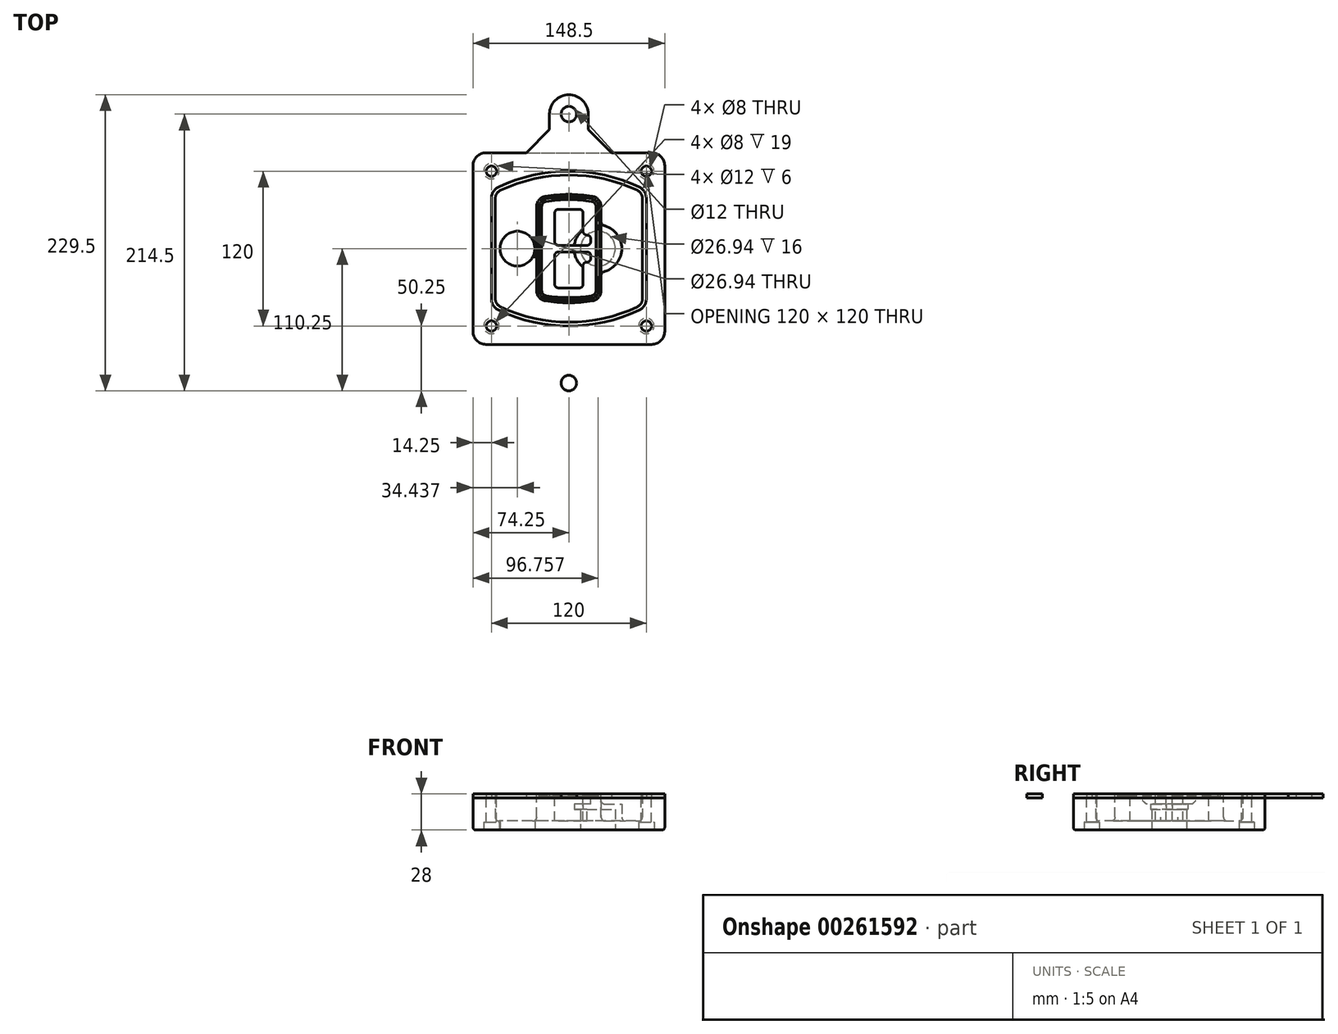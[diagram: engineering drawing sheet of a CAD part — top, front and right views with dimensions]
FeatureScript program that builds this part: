
annotation { "Feature Type Name" : "Feature", "Feature Type Description" : "" }
export const myFeature = defineFeature(function(context is Context, id is Id, definition is map)
    precondition{}
    {
        {
            var Q0;
            Q0=qCreatedBy(makeId("Top.planeOp"),FACE);
            var sketch = newSketch(context, id + "F0", { "sketchPlane" : qUnion([Q0])});
            skPoint(sketch, "E0.rect.middle", {"position": v(0, 0) * mm});
            skLineSegment(sketch, "E1.bottom", {"start": v(-64.25, -74.25) * mm, "end": v(64.25, -74.25) * mm});
            skLineSegment(sketch, "E1.top", {"start": v(-64.25, 74.25) * mm, "end": v(64.25, 74.25) * mm});
            skLineSegment(sketch, "E1.left", {"start": v(-74.25, -64.25) * mm, "end": v(-74.25, 64.25) * mm});
            skLineSegment(sketch, "E1.right", {"start": v(74.25, -64.25) * mm, "end": v(74.25, 64.25) * mm});
            skLineSegment(sketch, "E2", {"start": v(-74.25, 74.25) * mm, "end": v(74.25, -74.25) * mm, "construction": true});
            skLineSegment(sketch, "E3", {"start": v(74.25, 74.25) * mm, "end": v(-74.25, -74.25) * mm, "construction": true});
            skCircle(sketch, "E4", {"center": v(-60, 60) * mm, "radius": 4 * mm});
            skCircle(sketch, "E5", {"center": v(60, 60) * mm, "radius": 4 * mm});
            skCircle(sketch, "E6", {"center": v(60, -60) * mm, "radius": 4 * mm});
            skCircle(sketch, "E7", {"center": v(-60, -60) * mm, "radius": 4 * mm});
            skLineSegment(sketch, "E8", {"start": v(-60, 60) * mm, "end": v(60, 60) * mm, "construction": true});
            skLineSegment(sketch, "E9", {"start": v(60, 60) * mm, "end": v(60, -60) * mm, "construction": true});
            skLineSegment(sketch, "E10", {"start": v(60, -60) * mm, "end": v(-60, -60) * mm, "construction": true});
            skLineSegment(sketch, "E11", {"start": v(-60, -60) * mm, "end": v(-60, 60) * mm, "construction": true});
            skLineSegment(sketch, "E12", {"start": v(-60, 38.83) * mm, "end": v(-60, -38.83) * mm});
            skLineSegment(sketch, "E13", {"start": v(60, 38.83) * mm, "end": v(60, -38.83) * mm});
            skArc(sketch, "E14", {"start": v(54.26, 47.88) * mm, "mid": v(0, 60) * mm, "end": v(-54.26, 47.88) * mm});
            skArc(sketch, "E15", {"start": v(-54.26, -47.88) * mm, "mid": v(0, -60) * mm, "end": v(54.26, -47.88) * mm});
            skLineSegment(sketch, "E16", {"start": v(-60, 0) * mm, "end": v(60, 0) * mm, "construction": true});
            skPoint(sketch, "E17.visualSharp", {"position": v(-60, -45) * mm});
            skArc(sketch, "E17.filletArc", {"start": v(-60, -38.83) * mm, "mid": v(-58.44, -44.2) * mm, "end": v(-54.26, -47.88) * mm});
            skPoint(sketch, "E18.visualSharp", {"position": v(-60, 45) * mm});
            skArc(sketch, "E18.filletArc", {"start": v(-54.26, 47.88) * mm, "mid": v(-58.44, 44.2) * mm, "end": v(-60, 38.83) * mm});
            skPoint(sketch, "E19.visualSharp", {"position": v(60, 45) * mm});
            skArc(sketch, "E19.filletArc", {"start": v(60, 38.83) * mm, "mid": v(58.44, 44.2) * mm, "end": v(54.26, 47.88) * mm});
            skPoint(sketch, "E20.visualSharp", {"position": v(60, -45) * mm});
            skArc(sketch, "E20.filletArc", {"start": v(54.26, -47.88) * mm, "mid": v(58.44, -44.2) * mm, "end": v(60, -38.83) * mm});
            skPoint(sketch, "E21.visualSharp", {"position": v(-74.25, 74.25) * mm});
            skArc(sketch, "E21.filletArc", {"start": v(-64.25, 74.25) * mm, "mid": v(-71.32, 71.32) * mm, "end": v(-74.25, 64.25) * mm});
            skPoint(sketch, "E22.visualSharp", {"position": v(74.25, 74.25) * mm});
            skArc(sketch, "E22.filletArc", {"start": v(74.25, 64.25) * mm, "mid": v(71.32, 71.32) * mm, "end": v(64.25, 74.25) * mm});
            skPoint(sketch, "E23.visualSharp", {"position": v(74.25, -74.25) * mm});
            skArc(sketch, "E23.filletArc", {"start": v(64.25, -74.25) * mm, "mid": v(71.32, -71.32) * mm, "end": v(74.25, -64.25) * mm});
            skPoint(sketch, "E24.visualSharp", {"position": v(-74.25, -74.25) * mm});
            skArc(sketch, "E24.filletArc", {"start": v(-74.25, -64.25) * mm, "mid": v(-71.32, -71.32) * mm, "end": v(-64.25, -74.25) * mm});
            skArc(sketch, "E25.0", {"start": v(57, 38.83) * mm, "mid": v(55.9, 42.58) * mm, "end": v(52.98, 45.17) * mm});
            skLineSegment(sketch, "E25.1", {"start": v(57, 38.83) * mm, "end": v(57, -38.83) * mm});
            skArc(sketch, "E25.2", {"start": v(52.98, -45.17) * mm, "mid": v(55.9, -42.58) * mm, "end": v(57, -38.83) * mm});
            skArc(sketch, "E25.3", {"start": v(-52.98, -45.17) * mm, "mid": v(0, -57) * mm, "end": v(52.98, -45.17) * mm});
            skArc(sketch, "E25.4", {"start": v(-57, -38.83) * mm, "mid": v(-55.9, -42.58) * mm, "end": v(-52.98, -45.17) * mm});
            skArc(sketch, "E25.5", {"start": v(52.98, 45.17) * mm, "mid": v(0, 57) * mm, "end": v(-52.98, 45.17) * mm});
            skLineSegment(sketch, "E25.6", {"start": v(-57, 38.83) * mm, "end": v(-57, -38.83) * mm});
            skArc(sketch, "E25.7", {"start": v(-52.98, 45.17) * mm, "mid": v(-55.9, 42.58) * mm, "end": v(-57, 38.83) * mm});
            skArc(sketch, "E26.0", {"start": v(-55.96, 51.5) * mm, "mid": v(-61.82, 46.33) * mm, "end": v(-64, 38.83) * mm});
            skArc(sketch, "E26.1", {"start": v(55.96, 51.5) * mm, "mid": v(0, 64) * mm, "end": v(-55.96, 51.5) * mm});
            skArc(sketch, "E26.2", {"start": v(64, 38.83) * mm, "mid": v(61.82, 46.33) * mm, "end": v(55.96, 51.5) * mm});
            skLineSegment(sketch, "E26.3", {"start": v(64, 38.83) * mm, "end": v(64, -38.83) * mm});
            skArc(sketch, "E26.4", {"start": v(55.96, -51.5) * mm, "mid": v(61.82, -46.33) * mm, "end": v(64, -38.83) * mm});
            skLineSegment(sketch, "E26.5", {"start": v(-64, 38.83) * mm, "end": v(-64, -38.83) * mm});
            skArc(sketch, "E26.6", {"start": v(-55.96, -51.5) * mm, "mid": v(0, -64) * mm, "end": v(55.96, -51.5) * mm});
            skArc(sketch, "E26.7", {"start": v(-64, -38.83) * mm, "mid": v(-61.82, -46.33) * mm, "end": v(-55.96, -51.5) * mm});
            skSolve(sketch);
        }
        {
            var Q0;
            Q0=makeQuery(id+"F0.imprint","IMPRINT",FACE,{"disambiguationData":[TD([[makeQuery(id+"F0.imprint","IMPRINT",EDGE,{"derivedFrom":sQuery(id+"F0.wireOp",EDGE,"E1.bottom")}),1.0]])]});
            var Q1;
            Q1=makeQuery(id+"F0.imprint","IMPRINT",FACE,{"disambiguationData":[TD([[makeQuery(id+"F0.imprint","IMPRINT",EDGE,{"derivedFrom":sQuery(id+"F0.wireOp",EDGE,"E12")}),1.0]])]});
            var Q2;
            Q2=makeQuery(id+"F0.imprint","IMPRINT",FACE,{"disambiguationData":[TD([[makeQuery(id+"F0.imprint","IMPRINT",EDGE,{"derivedFrom":sQuery(id+"F0.wireOp",EDGE,"E25.0")}),1.0]])]});
            var Q3;
            Q3=makeQuery(id+"F0.imprint","IMPRINT",FACE,{"disambiguationData":[TD([[makeQuery(id+"F0.imprint","IMPRINT",EDGE,{"derivedFrom":sQuery(id+"F0.wireOp",EDGE,"E12")}),-1.0]])]});
            extrude(context, id + "F1", {"entities" : qUnion([Q0, Q1, Q2, Q3]), "oppositeDirection" : true, "depth" : 25 * mm});
        }
        {
            var Q0;
            Q0=makeQuery(id+"F0.imprint","IMPRINT",FACE,{"disambiguationData":[TD([[makeQuery(id+"F0.imprint","IMPRINT",EDGE,{"derivedFrom":sQuery(id+"F0.wireOp",EDGE,"E12")}),1.0]])]});
            extrude(context, id + "F2", {"entities" : qUnion([Q0]), "operationType" : NewBodyOperationType.ADD, "depth" : 3 * mm});
        }
        {
            var Q0;
            Q0=makeQuery(id+"F0.imprint","IMPRINT",FACE,{"disambiguationData":[TD([[makeQuery(id+"F0.imprint","IMPRINT",EDGE,{"derivedFrom":sQuery(id+"F0.wireOp",EDGE,"E25.0")}),1.0]])]});
            extrude(context, id + "F3", {"entities" : qUnion([Q0]), "operationType" : NewBodyOperationType.REMOVE, "oppositeDirection" : true, "depth" : 18 * mm});
        }
        {
            var Q0;
            Q0=makeQuery(id+"F2.opExtrude","CAP_FACE",FACE,{"disambiguationData":[OSD([sQuery(id+"F0.wireOp",EDGE,"E12"),sQuery(id+"F0.wireOp",EDGE,"E13"),sQuery(id+"F0.wireOp",EDGE,"E14"),sQuery(id+"F0.wireOp",EDGE,"E15"),sQuery(id+"F0.wireOp",EDGE,"E17.filletArc"),sQuery(id+"F0.wireOp",EDGE,"E18.filletArc"),sQuery(id+"F0.wireOp",EDGE,"E19.filletArc"),sQuery(id+"F0.wireOp",EDGE,"E20.filletArc"),sQuery(id+"F0.wireOp",EDGE,"E25.0"),sQuery(id+"F0.wireOp",EDGE,"E25.1"),sQuery(id+"F0.wireOp",EDGE,"E25.2"),sQuery(id+"F0.wireOp",EDGE,"E25.3"),sQuery(id+"F0.wireOp",EDGE,"E25.4"),sQuery(id+"F0.wireOp",EDGE,"E25.5"),sQuery(id+"F0.wireOp",EDGE,"E25.6"),sQuery(id+"F0.wireOp",EDGE,"E25.7")])],"isStart":false});
            var sketch = newSketch(context, id + "F4", { "sketchPlane" : qUnion([Q0])});
            skArc(sketch, "E27.0", {"start": v(-18.34, -40.45) * mm, "mid": v(0, -42) * mm, "end": v(18.34, -40.45) * mm});
            skArc(sketch, "E28.0", {"start": v(18.34, 40.45) * mm, "mid": v(0, 42) * mm, "end": v(-18.34, 40.45) * mm});
            skLineSegment(sketch, "E29", {"start": v(-25, 32.57) * mm, "end": v(-25, -32.57) * mm});
            skLineSegment(sketch, "E30", {"start": v(25, 32.57) * mm, "end": v(25, -32.57) * mm});
            skLineSegment(sketch, "E31", {"start": v(-25, 39.1) * mm, "end": v(25, 39.1) * mm, "construction": true});
            skLineSegment(sketch, "E32", {"start": v(-25, -39.1) * mm, "end": v(25, -39.1) * mm, "construction": true});
            skPoint(sketch, "E33.visualSharp", {"position": v(-25, 39.1) * mm});
            skArc(sketch, "E33.filletArc", {"start": v(-18.34, 40.45) * mm, "mid": v(-23.11, 37.73) * mm, "end": v(-25, 32.57) * mm});
            skPoint(sketch, "E34.visualSharp", {"position": v(25, 39.1) * mm});
            skArc(sketch, "E34.filletArc", {"start": v(25, 32.57) * mm, "mid": v(23.11, 37.73) * mm, "end": v(18.34, 40.45) * mm});
            skPoint(sketch, "E35.visualSharp", {"position": v(25, -39.1) * mm});
            skArc(sketch, "E35.filletArc", {"start": v(18.34, -40.45) * mm, "mid": v(23.11, -37.73) * mm, "end": v(25, -32.57) * mm});
            skPoint(sketch, "E36.visualSharp", {"position": v(-25, -39.1) * mm});
            skArc(sketch, "E36.filletArc", {"start": v(-25, -32.57) * mm, "mid": v(-23.11, -37.73) * mm, "end": v(-18.34, -40.45) * mm});
            skArc(sketch, "E37.0", {"start": v(52.98, 45.17) * mm, "mid": v(0, 57) * mm, "end": v(-52.98, 45.17) * mm});
            skArc(sketch, "E37.1", {"start": v(-52.98, 45.17) * mm, "mid": v(-55.9, 42.58) * mm, "end": v(-57, 38.83) * mm});
            skLineSegment(sketch, "E37.2", {"start": v(-57, 38.83) * mm, "end": v(-57, -38.83) * mm});
            skArc(sketch, "E37.3", {"start": v(-57, -38.83) * mm, "mid": v(-55.9, -42.58) * mm, "end": v(-52.98, -45.17) * mm});
            skArc(sketch, "E37.4", {"start": v(-52.98, -45.17) * mm, "mid": v(0, -57) * mm, "end": v(52.98, -45.17) * mm});
            skArc(sketch, "E37.5", {"start": v(52.98, -45.17) * mm, "mid": v(55.9, -42.58) * mm, "end": v(57, -38.83) * mm});
            skLineSegment(sketch, "E37.6", {"start": v(57, 38.83) * mm, "end": v(57, -38.83) * mm});
            skArc(sketch, "E37.7", {"start": v(57, 38.83) * mm, "mid": v(55.9, 42.58) * mm, "end": v(52.98, 45.17) * mm});
            skLineSegment(sketch, "E38.0", {"start": v(23, 32.57) * mm, "end": v(23, -32.57) * mm});
            skArc(sketch, "E38.1", {"start": v(18, -38.48) * mm, "mid": v(21.58, -36.44) * mm, "end": v(23, -32.57) * mm});
            skArc(sketch, "E38.2", {"start": v(-18, -38.48) * mm, "mid": v(0, -40) * mm, "end": v(18, -38.48) * mm});
            skArc(sketch, "E38.3", {"start": v(-23, -32.57) * mm, "mid": v(-21.58, -36.44) * mm, "end": v(-18, -38.48) * mm});
            skLineSegment(sketch, "E38.4", {"start": v(-23, 32.57) * mm, "end": v(-23, -32.57) * mm});
            skArc(sketch, "E38.5", {"start": v(23, 32.57) * mm, "mid": v(21.58, 36.44) * mm, "end": v(18, 38.48) * mm});
            skArc(sketch, "E38.6", {"start": v(-18, 38.48) * mm, "mid": v(-21.58, 36.44) * mm, "end": v(-23, 32.57) * mm});
            skArc(sketch, "E38.7", {"start": v(18, 38.48) * mm, "mid": v(0, 40) * mm, "end": v(-18, 38.48) * mm});
            skArc(sketch, "E39.0", {"start": v(21, 32.57) * mm, "mid": v(20.06, 35.15) * mm, "end": v(17.67, 36.5) * mm});
            skLineSegment(sketch, "E39.1", {"start": v(21, 32.57) * mm, "end": v(21, -32.57) * mm});
            skArc(sketch, "E39.2", {"start": v(17.67, -36.5) * mm, "mid": v(20.06, -35.15) * mm, "end": v(21, -32.57) * mm});
            skArc(sketch, "E39.3", {"start": v(-17.67, -36.5) * mm, "mid": v(0, -38) * mm, "end": v(17.67, -36.5) * mm});
            skArc(sketch, "E39.4", {"start": v(-21, -32.57) * mm, "mid": v(-20.06, -35.15) * mm, "end": v(-17.67, -36.5) * mm});
            skArc(sketch, "E39.5", {"start": v(17.67, 36.5) * mm, "mid": v(0, 38) * mm, "end": v(-17.67, 36.5) * mm});
            skLineSegment(sketch, "E39.6", {"start": v(-21, 32.57) * mm, "end": v(-21, -32.57) * mm});
            skArc(sketch, "E39.7", {"start": v(-17.67, 36.5) * mm, "mid": v(-20.06, 35.15) * mm, "end": v(-21, 32.57) * mm});
            skLineSegment(sketch, "E40", {"start": v(-25, 0) * mm, "end": v(25, 0) * mm, "construction": true});
            skLineSegment(sketch, "E41", {"start": v(-11, 5.5) * mm, "end": v(-11, 27.5) * mm});
            skLineSegment(sketch, "E42", {"start": v(-8, 30.5) * mm, "end": v(8, 30.5) * mm});
            skLineSegment(sketch, "E43", {"start": v(11, 27.5) * mm, "end": v(11, 13.5) * mm});
            skLineSegment(sketch, "E44", {"start": v(14, 10.5) * mm, "end": v(14, 10.5) * mm});
            skLineSegment(sketch, "E45", {"start": v(17, 7.5) * mm, "end": v(17, 5.5) * mm});
            skLineSegment(sketch, "E46", {"start": v(14, 2.5) * mm, "end": v(-8, 2.5) * mm});
            skPoint(sketch, "E47.visualSharp", {"position": v(-11, 30.5) * mm});
            skArc(sketch, "E47.filletArc", {"start": v(-8, 30.5) * mm, "mid": v(-10.12, 29.62) * mm, "end": v(-11, 27.5) * mm});
            skPoint(sketch, "E48.visualSharp", {"position": v(11, 30.5) * mm});
            skArc(sketch, "E48.filletArc", {"start": v(11, 27.5) * mm, "mid": v(10.12, 29.62) * mm, "end": v(8, 30.5) * mm});
            skPoint(sketch, "E49.visualSharp", {"position": v(11, 10.5) * mm});
            skArc(sketch, "E49.filletArc", {"start": v(11, 13.5) * mm, "mid": v(11.88, 11.38) * mm, "end": v(14, 10.5) * mm});
            skPoint(sketch, "E50.visualSharp", {"position": v(17, 10.5) * mm});
            skArc(sketch, "E50.filletArc", {"start": v(17, 7.5) * mm, "mid": v(16.12, 9.62) * mm, "end": v(14, 10.5) * mm});
            skPoint(sketch, "E51.visualSharp", {"position": v(17, 2.5) * mm});
            skArc(sketch, "E51.filletArc", {"start": v(14, 2.5) * mm, "mid": v(16.12, 3.38) * mm, "end": v(17, 5.5) * mm});
            skPoint(sketch, "E52.visualSharp", {"position": v(-11, 2.5) * mm});
            skArc(sketch, "E52.filletArc", {"start": v(-11, 5.5) * mm, "mid": v(-10.12, 3.38) * mm, "end": v(-8, 2.5) * mm});
            skLineSegment(sketch, "E53.0.MirrorCS", {"start": v(14, -2.5) * mm, "end": v(-8, -2.5) * mm});
            skArc(sketch, "E54.0.MirrorCS", {"start": v(-11, -5.5) * mm, "mid": v(-10.12, -3.38) * mm, "end": v(-8, -2.5) * mm});
            skLineSegment(sketch, "E55.0.MirrorCS", {"start": v(-11, -5.5) * mm, "end": v(-11, -27.5) * mm});
            skArc(sketch, "E56.0.MirrorCS", {"start": v(-8, -30.5) * mm, "mid": v(-10.12, -29.62) * mm, "end": v(-11, -27.5) * mm});
            skLineSegment(sketch, "E57.0.MirrorCS", {"start": v(-8, -30.5) * mm, "end": v(8, -30.5) * mm});
            skArc(sketch, "E58.0.MirrorCS", {"start": v(11, -27.5) * mm, "mid": v(10.12, -29.62) * mm, "end": v(8, -30.5) * mm});
            skLineSegment(sketch, "E59.0.MirrorCS", {"start": v(11, -27.5) * mm, "end": v(11, -13.5) * mm});
            skArc(sketch, "E60.0.MirrorCS", {"start": v(11, -13.5) * mm, "mid": v(11.88, -11.38) * mm, "end": v(14, -10.5) * mm});
            skArc(sketch, "E61.0.MirrorCS", {"start": v(17, -7.5) * mm, "mid": v(16.12, -9.62) * mm, "end": v(14, -10.5) * mm});
            skLineSegment(sketch, "E62.0.MirrorCS", {"start": v(17, -7.5) * mm, "end": v(17, -5.5) * mm});
            skArc(sketch, "E63.0.MirrorCS", {"start": v(14, -2.5) * mm, "mid": v(16.12, -3.38) * mm, "end": v(17, -5.5) * mm});
            skSolve(sketch);
        }
        {
            var Q0;
            Q0=makeQuery(id+"F4.imprint","IMPRINT",FACE,{"disambiguationData":[TD([[makeQuery(id+"F4.imprint","IMPRINT",EDGE,{"derivedFrom":sQuery(id+"F4.wireOp",EDGE,"E27.0")}),1.0]])]});
            var Q1;
            Q1=makeQuery(id+"F4.imprint","IMPRINT",FACE,{"disambiguationData":[TD([[makeQuery(id+"F4.imprint","IMPRINT",EDGE,{"derivedFrom":sQuery(id+"F4.wireOp",EDGE,"E38.0")}),-1.0]])]});
            var Q2;
            Q2=makeQuery(id+"F4.imprint","IMPRINT",FACE,{"disambiguationData":[TD([[makeQuery(id+"F4.imprint","IMPRINT",EDGE,{"derivedFrom":sQuery(id+"F4.wireOp",EDGE,"E39.0")}),1.0]])]});
            extrude(context, id + "F5", {"entities" : qUnion([Q0, Q1, Q2]), "operationType" : NewBodyOperationType.ADD, "endBound" : BoundingType.UP_TO_NEXT, "oppositeDirection" : true, "depth" : 25 * mm});
        }
        {
            var Q0;
            Q0=makeQuery(id+"F4.imprint","IMPRINT",FACE,{"disambiguationData":[TD([[makeQuery(id+"F4.imprint","IMPRINT",EDGE,{"derivedFrom":sQuery(id+"F4.wireOp",EDGE,"E38.0")}),-1.0]])]});
            extrude(context, id + "F6", {"entities" : qUnion([Q0]), "operationType" : NewBodyOperationType.REMOVE, "oppositeDirection" : true, "depth" : 2 * mm});
        }
        {
            var Q0;
            Q0=makeQuery(id+"F1.opExtrude","CAP_FACE",FACE,{"disambiguationData":[OSD([sQuery(id+"F0.wireOp",EDGE,"E1.bottom"),sQuery(id+"F0.wireOp",EDGE,"E1.top"),sQuery(id+"F0.wireOp",EDGE,"E1.left"),sQuery(id+"F0.wireOp",EDGE,"E1.right"),sQuery(id+"F0.wireOp",EDGE,"E4"),sQuery(id+"F0.wireOp",EDGE,"E5"),sQuery(id+"F0.wireOp",EDGE,"E6"),sQuery(id+"F0.wireOp",EDGE,"E7"),sQuery(id+"F0.wireOp",EDGE,"E21.filletArc"),sQuery(id+"F0.wireOp",EDGE,"E22.filletArc"),sQuery(id+"F0.wireOp",EDGE,"E23.filletArc"),sQuery(id+"F0.wireOp",EDGE,"E24.filletArc")])],"isStart":false});
            var sketch = newSketch(context, id + "F7", { "sketchPlane" : qUnion([Q0])});
            skCircle(sketch, "E64", {"center": v(22.5, 0) * mm, "radius": 13.47 * mm});
            skCircle(sketch, "E65", {"center": v(-39.81, 0) * mm, "radius": 13.47 * mm});
            skLineSegment(sketch, "E66", {"start": v(74.25, 0) * mm, "end": v(-74.25, 0) * mm});
            skCircle(sketch, "E67", {"center": v(22.5, 0) * mm, "radius": 18.47 * mm});
            skCircle(sketch, "E68", {"center": v(60, -60) * mm, "radius": 6 * mm});
            skCircle(sketch, "E69", {"center": v(-60, -60) * mm, "radius": 6 * mm});
            skCircle(sketch, "E70", {"center": v(-60, 60) * mm, "radius": 6 * mm});
            skCircle(sketch, "E71", {"center": v(60, 60) * mm, "radius": 6 * mm});
            skSolve(sketch);
        }
        {
            var Q0;
            {var subQ1=sQuery(id+"F7.wireOp",EDGE,"E66");var subQ4=sQuery(id+"F7.wireOp",EDGE,"E64");var subQ6=makeQuery(id+"F7.imprint","INTERSECT",VERTEX,{"disambiguationData":[OD(0.0)],"derivedFrom":[subQ4,subQ1]});Q0=makeQuery(id+"F7.imprint","IMPRINT",FACE,{"disambiguationData":[TD([[makeQuery(id+"F7.imprint","IMPRINT",EDGE,{"disambiguationData":[TD([[subQ6,-1.0]])],"derivedFrom":subQ4}),-1.0]])]});}
            var Q1;
            {var subQ0=sQuery(id+"F7.wireOp",EDGE,"E66");var subQ1=sQuery(id+"F7.wireOp",EDGE,"E64");var subQ3=makeQuery(id+"F7.imprint","INTERSECT",VERTEX,{"disambiguationData":[OD(0.0)],"derivedFrom":[subQ1,subQ0]});Q1=makeQuery(id+"F7.imprint","IMPRINT",FACE,{"disambiguationData":[TD([[makeQuery(id+"F7.imprint","IMPRINT",EDGE,{"disambiguationData":[TD([[subQ3,-1.0]])],"derivedFrom":subQ1}),1.0]])]});}
            var Q2;
            {var subQ0=sQuery(id+"F7.wireOp",EDGE,"E66");var subQ1=sQuery(id+"F7.wireOp",EDGE,"E64");var subQ3=makeQuery(id+"F7.imprint","INTERSECT",VERTEX,{"disambiguationData":[OD(0.0)],"derivedFrom":[subQ1,subQ0]});Q2=makeQuery(id+"F7.imprint","IMPRINT",FACE,{"disambiguationData":[TD([[makeQuery(id+"F7.imprint","IMPRINT",EDGE,{"disambiguationData":[TD([[subQ3,1.0]])],"derivedFrom":subQ1}),1.0]])]});}
            var Q3;
            {var subQ1=sQuery(id+"F7.wireOp",EDGE,"E66");var subQ4=sQuery(id+"F7.wireOp",EDGE,"E64");var subQ6=makeQuery(id+"F7.imprint","INTERSECT",VERTEX,{"disambiguationData":[OD(0.0)],"derivedFrom":[subQ4,subQ1]});Q3=makeQuery(id+"F7.imprint","IMPRINT",FACE,{"disambiguationData":[TD([[makeQuery(id+"F7.imprint","IMPRINT",EDGE,{"disambiguationData":[TD([[subQ6,1.0]])],"derivedFrom":subQ4}),-1.0]])]});}
            extrude(context, id + "F8", {"entities" : qUnion([Q0, Q1, Q2, Q3]), "operationType" : NewBodyOperationType.ADD, "oppositeDirection" : true, "depth" : 20 * mm});
        }
        {
            var Q0;
            {var subQ0=sQuery(id+"F7.wireOp",EDGE,"E66");var subQ1=sQuery(id+"F7.wireOp",EDGE,"E64");var subQ3=makeQuery(id+"F7.imprint","INTERSECT",VERTEX,{"disambiguationData":[OD(0.0)],"derivedFrom":[subQ1,subQ0]});Q0=makeQuery(id+"F7.imprint","IMPRINT",FACE,{"disambiguationData":[TD([[makeQuery(id+"F7.imprint","IMPRINT",EDGE,{"disambiguationData":[TD([[subQ3,-1.0]])],"derivedFrom":subQ1}),1.0]])]});}
            var Q1;
            {var subQ0=sQuery(id+"F7.wireOp",EDGE,"E66");var subQ1=sQuery(id+"F7.wireOp",EDGE,"E64");var subQ3=makeQuery(id+"F7.imprint","INTERSECT",VERTEX,{"disambiguationData":[OD(0.0)],"derivedFrom":[subQ1,subQ0]});Q1=makeQuery(id+"F7.imprint","IMPRINT",FACE,{"disambiguationData":[TD([[makeQuery(id+"F7.imprint","IMPRINT",EDGE,{"disambiguationData":[TD([[subQ3,1.0]])],"derivedFrom":subQ1}),1.0]])]});}
            extrude(context, id + "F9", {"entities" : qUnion([Q0, Q1]), "operationType" : NewBodyOperationType.REMOVE, "oppositeDirection" : true, "depth" : 16 * mm});
        }
        {
            var Q0;
            {var subQ0=sQuery(id+"F7.wireOp",EDGE,"E66");var subQ1=sQuery(id+"F7.wireOp",EDGE,"E65");var subQ3=makeQuery(id+"F7.imprint","INTERSECT",VERTEX,{"disambiguationData":[OD(0.0)],"derivedFrom":[subQ1,subQ0]});Q0=makeQuery(id+"F7.imprint","IMPRINT",FACE,{"disambiguationData":[TD([[makeQuery(id+"F7.imprint","IMPRINT",EDGE,{"disambiguationData":[TD([[subQ3,-1.0]])],"derivedFrom":subQ1}),1.0]])]});}
            var Q1;
            {var subQ0=sQuery(id+"F7.wireOp",EDGE,"E66");var subQ1=sQuery(id+"F7.wireOp",EDGE,"E65");var subQ3=makeQuery(id+"F7.imprint","INTERSECT",VERTEX,{"disambiguationData":[OD(0.0)],"derivedFrom":[subQ1,subQ0]});Q1=makeQuery(id+"F7.imprint","IMPRINT",FACE,{"disambiguationData":[TD([[makeQuery(id+"F7.imprint","IMPRINT",EDGE,{"disambiguationData":[TD([[subQ3,1.0]])],"derivedFrom":subQ1}),1.0]])]});}
            extrude(context, id + "F10", {"entities" : qUnion([Q0, Q1]), "operationType" : NewBodyOperationType.REMOVE, "oppositeDirection" : true, "depth" : 25 * mm});
        }
        {
            var Q0;
            Q0=makeQuery(id+"F7.imprint","IMPRINT",FACE,{"disambiguationData":[TD([[makeQuery(id+"F7.imprint","IMPRINT",EDGE,{"derivedFrom":sQuery(id+"F7.wireOp",EDGE,"E68")}),1.0]])]});
            var Q1;
            Q1=makeQuery(id+"F7.imprint","IMPRINT",FACE,{"disambiguationData":[TD([[makeQuery(id+"F7.imprint","IMPRINT",EDGE,{"derivedFrom":makeQuery(id+"F1.opExtrude","CAP_EDGE",EDGE,{"disambiguationData":[OSD([sQuery(id+"F0.wireOp",EDGE,"E5")])],"isStart":false})}),-1.0]])]});
            var Q2;
            Q2=makeQuery(id+"F7.imprint","IMPRINT",FACE,{"disambiguationData":[TD([[makeQuery(id+"F7.imprint","IMPRINT",EDGE,{"derivedFrom":sQuery(id+"F7.wireOp",EDGE,"E69")}),1.0]])]});
            var Q3;
            Q3=makeQuery(id+"F7.imprint","IMPRINT",FACE,{"disambiguationData":[TD([[makeQuery(id+"F7.imprint","IMPRINT",EDGE,{"derivedFrom":makeQuery(id+"F1.opExtrude","CAP_EDGE",EDGE,{"disambiguationData":[OSD([sQuery(id+"F0.wireOp",EDGE,"E4")])],"isStart":false})}),-1.0]])]});
            var Q4;
            Q4=makeQuery(id+"F7.imprint","IMPRINT",FACE,{"disambiguationData":[TD([[makeQuery(id+"F7.imprint","IMPRINT",EDGE,{"derivedFrom":sQuery(id+"F7.wireOp",EDGE,"E70")}),1.0]])]});
            var Q5;
            Q5=makeQuery(id+"F7.imprint","IMPRINT",FACE,{"disambiguationData":[TD([[makeQuery(id+"F7.imprint","IMPRINT",EDGE,{"derivedFrom":makeQuery(id+"F1.opExtrude","CAP_EDGE",EDGE,{"disambiguationData":[OSD([sQuery(id+"F0.wireOp",EDGE,"E7")])],"isStart":false})}),-1.0]])]});
            var Q6;
            Q6=makeQuery(id+"F7.imprint","IMPRINT",FACE,{"disambiguationData":[TD([[makeQuery(id+"F7.imprint","IMPRINT",EDGE,{"derivedFrom":sQuery(id+"F7.wireOp",EDGE,"E71")}),1.0]])]});
            var Q7;
            Q7=makeQuery(id+"F7.imprint","IMPRINT",FACE,{"disambiguationData":[TD([[makeQuery(id+"F7.imprint","IMPRINT",EDGE,{"derivedFrom":makeQuery(id+"F1.opExtrude","CAP_EDGE",EDGE,{"disambiguationData":[OSD([sQuery(id+"F0.wireOp",EDGE,"E6")])],"isStart":false})}),-1.0]])]});
            extrude(context, id + "F11", {"entities" : qUnion([Q0, Q1, Q2, Q3, Q4, Q5, Q6, Q7]), "operationType" : NewBodyOperationType.REMOVE, "oppositeDirection" : true, "depth" : 6 * mm});
        }
        {
            var Q0;
            Q0=makeQuery(id+"F9.boolean.opBoolean","COPY",FACE,{"derivedFrom":makeQuery(id+"F9.opExtrude","CAP_FACE",FACE,{"disambiguationData":[OSD([sQuery(id+"F7.wireOp",EDGE,"E64")])],"isStart":false})});
            var sketch = newSketch(context, id + "F12", { "sketchPlane" : qUnion([Q0])});
            skArc(sketch, "E72.0", {"start": v(11, 14.45) * mm, "mid": v(6.45, 9.13) * mm, "end": v(4.2, 2.5) * mm});
            skArc(sketch, "E72.1", {"start": v(4.2, -2.5) * mm, "mid": v(6.45, -9.13) * mm, "end": v(11, -14.45) * mm});
            skLineSegment(sketch, "E73", {"start": v(4.2, -2.5) * mm, "end": v(14, -2.5) * mm});
            skLineSegment(sketch, "E74.0", {"start": v(14, 2.5) * mm, "end": v(4.2, 2.5) * mm});
            skArc(sketch, "E74.1", {"start": v(14, 2.5) * mm, "mid": v(16.12, 3.38) * mm, "end": v(17, 5.5) * mm});
            skLineSegment(sketch, "E74.2", {"start": v(17, 7.5) * mm, "end": v(17, 5.5) * mm});
            skArc(sketch, "E74.3", {"start": v(17, 7.5) * mm, "mid": v(16.12, 9.62) * mm, "end": v(14, 10.5) * mm});
            skArc(sketch, "E74.4", {"start": v(11, 13.5) * mm, "mid": v(11.88, 11.38) * mm, "end": v(14, 10.5) * mm});
            skLineSegment(sketch, "E74.5", {"start": v(11, 14.45) * mm, "end": v(11, 13.5) * mm});
            skLineSegment(sketch, "E74.7", {"start": v(14, -2.5) * mm, "end": v(4.2, -2.5) * mm});
            skArc(sketch, "E74.8", {"start": v(14, -2.5) * mm, "mid": v(16.12, -3.38) * mm, "end": v(17, -5.5) * mm});
            skLineSegment(sketch, "E74.9", {"start": v(17, -7.5) * mm, "end": v(17, -5.5) * mm});
            skArc(sketch, "E74.10", {"start": v(17, -7.5) * mm, "mid": v(16.12, -9.62) * mm, "end": v(14, -10.5) * mm});
            skArc(sketch, "E74.11", {"start": v(11, -13.5) * mm, "mid": v(11.88, -11.38) * mm, "end": v(14, -10.5) * mm});
            skLineSegment(sketch, "E74.12", {"start": v(11, -14.45) * mm, "end": v(11, -13.5) * mm});
            skPoint(sketch, "E75.orphan", {"position": v(11, -27.5) * mm});
            skPoint(sketch, "E76.orphan", {"position": v(-8, -2.5) * mm});
            skPoint(sketch, "E77.orphan", {"position": v(-8, 2.5) * mm});
            skPoint(sketch, "E78.orphan", {"position": v(11, 27.5) * mm});
            skSolve(sketch);
        }
        {
            var Q0;
            {var subQ7=sQuery(id+"F12.wireOp",EDGE,"E72.0");var subQ14=sQuery(id+"F12.wireOp",EDGE,"E72.1");var subQ16=sQuery(id+"F12.wireOp",EDGE,"E74.1");var subQ18=sQuery(id+"F12.wireOp",EDGE,"E74.8");Q0=qUnion([makeQuery(id+"F12.imprint","IMPRINT",FACE,{"disambiguationData":[TD([[makeQuery(id+"F12.imprint","IMPRINT",EDGE,{"derivedFrom":subQ7}),1.0]])]}),makeQuery(id+"F12.imprint","IMPRINT",FACE,{"disambiguationData":[TD([[makeQuery(id+"F12.imprint","IMPRINT",EDGE,{"derivedFrom":subQ14}),1.0]])]}),makeQuery(id+"F12.imprint","IMPRINT",FACE,{"disambiguationData":[TD([[makeQuery(id+"F12.imprint","IMPRINT",EDGE,{"derivedFrom":subQ16}),1.0]])]}),makeQuery(id+"F12.imprint","IMPRINT",FACE,{"disambiguationData":[TD([[makeQuery(id+"F12.imprint","IMPRINT",EDGE,{"derivedFrom":subQ18}),-1.0]])]})]);}
            var Q1;
            Q1=makeQuery(id+"F5.boolean.opBoolean","SPLIT",FACE,{"disambiguationData":[TD([makeQuery(id+"F5.opExtrude","SWEPT_FACE",FACE,{"disambiguationData":[OSD([sQuery(id+"F4.wireOp",EDGE,"E41")])]})])],"derivedFrom":makeQuery(id+"F3.boolean.opBoolean","COPY",FACE,{"derivedFrom":makeQuery(id+"F3.opExtrude","CAP_FACE",FACE,{"disambiguationData":[OSD([sQuery(id+"F0.wireOp",EDGE,"E25.0"),sQuery(id+"F0.wireOp",EDGE,"E25.1"),sQuery(id+"F0.wireOp",EDGE,"E25.2"),sQuery(id+"F0.wireOp",EDGE,"E25.3"),sQuery(id+"F0.wireOp",EDGE,"E25.4"),sQuery(id+"F0.wireOp",EDGE,"E25.5"),sQuery(id+"F0.wireOp",EDGE,"E25.6"),sQuery(id+"F0.wireOp",EDGE,"E25.7")])],"isStart":false})})});
            extrude(context, id + "F13", {"entities" : qUnion([Q0]), "operationType" : NewBodyOperationType.REMOVE, "endBound" : BoundingType.UP_TO_SURFACE, "endBoundEntityFace" : qUnion([Q1]), "depth" : 25 * mm});
        }
        {
            var Q0;
            Q0=makeQuery(id+"F3.boolean.opBoolean","COPY",EDGE,{"derivedFrom":makeQuery(id+"F3.opExtrude","CAP_EDGE",EDGE,{"disambiguationData":[OSD([sQuery(id+"F0.wireOp",EDGE,"E25.6")])],"isStart":false})});
            var Q1;
            Q1=makeQuery(id+"F8.boolean.opBoolean","INTERSECT",EDGE,{"derivedFrom":[makeQuery(id+"F5.opExtrude","SWEPT_FACE",FACE,{"disambiguationData":[OSD([sQuery(id+"F4.wireOp",EDGE,"E30")])]}),makeQuery(id+"F8.opExtrude","CAP_FACE",FACE,{"disambiguationData":[OSD([sQuery(id+"F7.wireOp",EDGE,"E67")])],"isStart":false})]});
            var Q2;
            Q2=makeQuery(id+"F8.boolean.opBoolean","INTERSECT",EDGE,{"disambiguationData":[OD(1.0)],"derivedFrom":[makeQuery(id+"F5.opExtrude","SWEPT_FACE",FACE,{"disambiguationData":[OSD([sQuery(id+"F4.wireOp",EDGE,"E30")])]}),makeQuery(id+"F8.opExtrude","SWEPT_FACE",FACE,{"disambiguationData":[OSD([sQuery(id+"F7.wireOp",EDGE,"E67")])]})]});
            var Q3;
            {var subQ0=sQuery(id+"F4.wireOp",EDGE,"E30");Q3=makeQuery(id+"F8.boolean.opBoolean","SPLIT",EDGE,{"disambiguationData":[TD([makeQuery(id+"F5.opExtrude","SWEPT_FACE",FACE,{"disambiguationData":[OSD([sQuery(id+"F4.wireOp",EDGE,"E35.filletArc")])]})])],"derivedFrom":makeQuery(id+"F5.opExtrude","CAP_EDGE",EDGE,{"disambiguationData":[OSD([subQ0])],"isStart":false})});}
            var Q4;
            {var subQ0=sQuery(id+"F0.wireOp",EDGE,"E25.7");var subQ1=sQuery(id+"F0.wireOp",EDGE,"E25.1");var subQ2=sQuery(id+"F0.wireOp",EDGE,"E25.6");var subQ3=sQuery(id+"F0.wireOp",EDGE,"E25.5");var subQ4=sQuery(id+"F0.wireOp",EDGE,"E25.4");var subQ5=sQuery(id+"F0.wireOp",EDGE,"E25.0");var subQ6=sQuery(id+"F0.wireOp",EDGE,"E25.2");var subQ7=sQuery(id+"F0.wireOp",EDGE,"E25.3");Q4=makeQuery(id+"F8.boolean.opBoolean","INTERSECT",EDGE,{"derivedFrom":[makeQuery(id+"F5.boolean.opBoolean","SPLIT",FACE,{"disambiguationData":[TD([makeQuery(id+"F2.opExtrude","SWEPT_FACE",FACE,{"disambiguationData":[OSD([subQ5])]})])],"derivedFrom":makeQuery(id+"F3.boolean.opBoolean","COPY",FACE,{"derivedFrom":makeQuery(id+"F3.opExtrude","CAP_FACE",FACE,{"disambiguationData":[OSD([subQ5,subQ1,subQ6,subQ7,subQ4,subQ3,subQ2,subQ0])],"isStart":false})})}),makeQuery(id+"F8.opExtrude","SWEPT_FACE",FACE,{"disambiguationData":[OSD([sQuery(id+"F7.wireOp",EDGE,"E67")])]})]});}
            var Q5;
            Q5=makeQuery(id+"F8.boolean.opBoolean","INTERSECT",EDGE,{"disambiguationData":[OD(0.0)],"derivedFrom":[makeQuery(id+"F5.opExtrude","SWEPT_FACE",FACE,{"disambiguationData":[OSD([sQuery(id+"F4.wireOp",EDGE,"E30")])]}),makeQuery(id+"F8.opExtrude","SWEPT_FACE",FACE,{"disambiguationData":[OSD([sQuery(id+"F7.wireOp",EDGE,"E67")])]})]});
            fillet(context, id + "F14", {"entities" : qUnion([Q0, Q1, Q2, Q3, Q4, Q5]), "radius" : 3 * mm, "tangentPropagation" : true, "allowEdgeOverflow" : false});
        }
        {
            var Q0;
            Q0=makeQuery(id+"F1.opExtrude","CAP_EDGE",EDGE,{"disambiguationData":[OSD([sQuery(id+"F0.wireOp",EDGE,"E1.bottom")])],"isStart":false});
            fillet(context, id + "F15", {"entities" : qUnion([Q0]), "radius" : 2 * mm, "tangentPropagation" : true, "allowEdgeOverflow" : false});
        }
        {
            var Q0;
            {var subQ0=sQuery(id+"F0.wireOp",EDGE,"E22.filletArc");var subQ1=sQuery(id+"F0.wireOp",EDGE,"E7");var subQ2=sQuery(id+"F0.wireOp",EDGE,"E6");var subQ3=sQuery(id+"F0.wireOp",EDGE,"E5");var subQ4=sQuery(id+"F0.wireOp",EDGE,"E4");var subQ5=sQuery(id+"F0.wireOp",EDGE,"E1.bottom");var subQ6=sQuery(id+"F0.wireOp",EDGE,"E21.filletArc");var subQ7=sQuery(id+"F0.wireOp",EDGE,"E1.top");var subQ8=sQuery(id+"F0.wireOp",EDGE,"E1.left");var subQ9=sQuery(id+"F0.wireOp",EDGE,"E1.right");var subQ10=sQuery(id+"F0.wireOp",EDGE,"E23.filletArc");var subQ11=sQuery(id+"F0.wireOp",EDGE,"E24.filletArc");Q0=makeQuery(id+"F2.boolean.opBoolean","SPLIT",FACE,{"disambiguationData":[TD([makeQuery(id+"F1.opExtrude","SWEPT_FACE",FACE,{"disambiguationData":[OSD([subQ5])]})])],"derivedFrom":makeQuery(id+"F1.opExtrude","CAP_FACE",FACE,{"disambiguationData":[OSD([subQ5,subQ7,subQ8,subQ9,subQ4,subQ3,subQ2,subQ1,subQ6,subQ0,subQ10,subQ11])],"isStart":true})});}
            var sketch = newSketch(context, id + "F16", { "sketchPlane" : qUnion([Q0])});
            skCircle(sketch, "E79", {"center": v(0, 104.25) * mm, "radius": 6 * mm});
            skPoint(sketch, "E79.centerSnap0", {"position": v(0, 74.25) * mm});
            skLineSegment(sketch, "E80", {"start": v(0, 104.25) * mm, "end": v(0, 74.25) * mm, "construction": true});
            skLineSegment(sketch, "E81", {"start": v(-33, 74.25) * mm, "end": v(-15, 92.25) * mm});
            skLineSegment(sketch, "E82", {"start": v(-15, 92.25) * mm, "end": v(-15, 104.25) * mm});
            skLineSegment(sketch, "E83", {"start": v(15, 104.25) * mm, "end": v(15, 92.25) * mm});
            skLineSegment(sketch, "E84", {"start": v(15, 92.25) * mm, "end": v(33, 74.25) * mm});
            skArc(sketch, "E85", {"start": v(15, 104.25) * mm, "mid": v(0, 119.25) * mm, "end": v(-15, 104.25) * mm});
            skLineSegment(sketch, "E86", {"start": v(-74.25, 0) * mm, "end": v(74.25, 0) * mm, "construction": true});
            skLineSegment(sketch, "E87", {"start": v(-64.25, 74.25) * mm, "end": v(64.25, 74.25) * mm});
            skLineSegment(sketch, "E88", {"start": v(74.25, 64.25) * mm, "end": v(74.25, 0) * mm});
            skLineSegment(sketch, "E89", {"start": v(-74.25, 64.25) * mm, "end": v(-74.25, 0) * mm});
            skArc(sketch, "E90", {"start": v(-74.25, 64.25) * mm, "mid": v(-71.32, 71.32) * mm, "end": v(-64.25, 74.25) * mm});
            skArc(sketch, "E91", {"start": v(64.25, 74.25) * mm, "mid": v(71.32, 71.32) * mm, "end": v(74.25, 64.25) * mm});
            skLineSegment(sketch, "E92.MirrorCS", {"start": v(-74.25, -64.25) * mm, "end": v(-74.25, 0) * mm});
            skArc(sketch, "E93.MirrorCS", {"start": v(-74.25, -64.25) * mm, "mid": v(-71.32, -71.32) * mm, "end": v(-64.25, -74.25) * mm});
            skLineSegment(sketch, "E94.MirrorCS", {"start": v(-64.25, -74.25) * mm, "end": v(64.25, -74.25) * mm});
            skArc(sketch, "E95.MirrorCS", {"start": v(64.25, -74.25) * mm, "mid": v(71.32, -71.32) * mm, "end": v(74.25, -64.25) * mm});
            skLineSegment(sketch, "E96.MirrorCS", {"start": v(74.25, -64.25) * mm, "end": v(74.25, 0) * mm});
            skCircle(sketch, "E97.MirrorC", {"center": v(0, -104.25) * mm, "radius": 6 * mm});
            skArc(sketch, "E98.MirrorCS", {"start": v(15, -104.25) * mm, "mid": v(0, -119.25) * mm, "end": v(-15, -104.25) * mm});
            skLineSegment(sketch, "E99.MirrorCS", {"start": v(-15, -92.25) * mm, "end": v(-15, -104.25) * mm});
            skLineSegment(sketch, "E100.MirrorCS", {"start": v(15, -104.25) * mm, "end": v(15, -92.25) * mm});
            skLineSegment(sketch, "E101.MirrorCS", {"start": v(15, -92.25) * mm, "end": v(33, -74.25) * mm});
            skLineSegment(sketch, "E102.MirrorCS", {"start": v(-33, -74.25) * mm, "end": v(-15, -92.25) * mm});
            skSolve(sketch);
        }
        {
            var Q0;
            Q0=makeQuery(id+"F16.imprint","IMPRINT",FACE,{"disambiguationData":[TD([[makeQuery(id+"F16.imprint","IMPRINT",EDGE,{"derivedFrom":sQuery(id+"F16.wireOp",EDGE,"E97.MirrorC")}),1.0]])]});
            var Q1;
            Q1=makeQuery(id+"F16.imprint","IMPRINT",FACE,{"disambiguationData":[TD([[makeQuery(id+"F16.imprint","IMPRINT",EDGE,{"derivedFrom":sQuery(id+"F16.wireOp",EDGE,"E79")}),-1.0]])]});
            var Q2;
            Q2=makeQuery(id+"F16.imprint","IMPRINT",FACE,{"disambiguationData":[TD([[makeQuery(id+"F16.imprint","IMPRINT",EDGE,{"derivedFrom":sQuery(id+"F16.wireOp",EDGE,"E88")}),1.0]])]});
            extrude(context, id + "F17", {"entities" : qUnion([Q0, Q1, Q2]), "depth" : 3 * mm});
        }
    });
